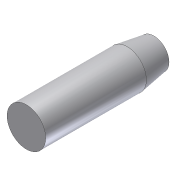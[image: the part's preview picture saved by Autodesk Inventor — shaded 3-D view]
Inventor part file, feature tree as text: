
AUTODESK INVENTOR PART (.ipt)
format: ipt  version: 2012 (Build 160160000, 160)  size: 80,384 bytes
history: native  units: in
note: dims shown in document units (in); Inventor stores cm internally (conversion verified against a paired STEP export)
features: extrude x1, chamfer x1, sketch x1
ambient origin geometry x8: Origin, YZ Plane, XZ Plane, XY Plane, X Axis, Y Axis, Z Axis, Center Point
bodies: Solid1 (feature_tree)
feature tree (3):
  extrude  "Extrusion1"  Depth=4.75in TaperAngle=0.0deg
  chamfer  "Chamfer1"  Distance=0.1562in Angle=45.0deg
  sketch  "Sketch1"  dims[d0=1.4375in d1=4.75in d2=0.0in d3=0.1562in d4=1.0in d5=45.0deg]
